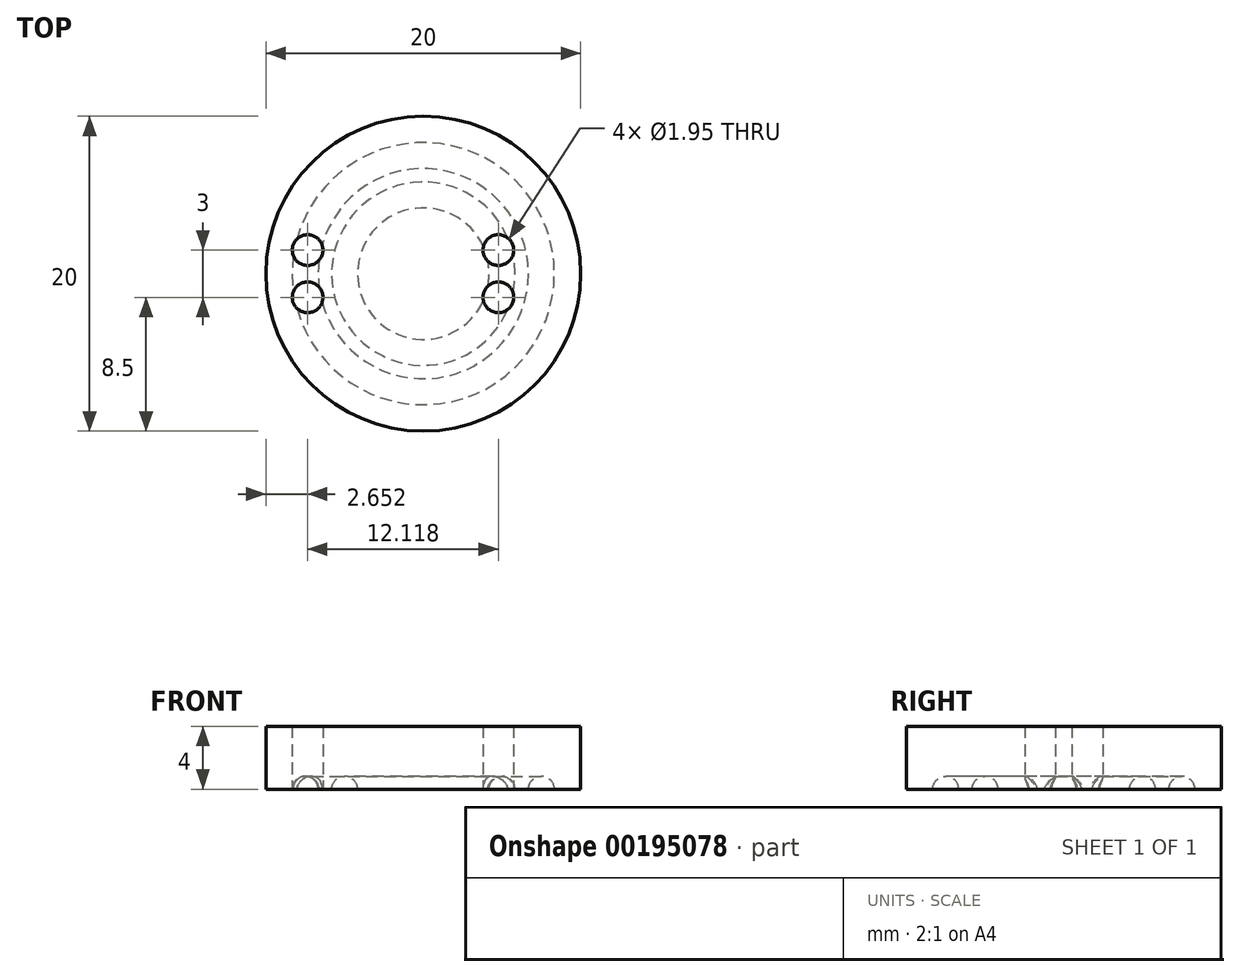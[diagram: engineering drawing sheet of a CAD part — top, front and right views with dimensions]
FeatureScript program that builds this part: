
annotation { "Feature Type Name" : "Feature", "Feature Type Description" : "" }
export const myFeature = defineFeature(function(context is Context, id is Id, definition is map)
    precondition{}
    {
        {
            assignVariable(context, id + "F0", {"name" : "thick", "anyValue" : 4});
        }
        {
            var Q0;
            Q0=qCreatedBy(makeId("Top.planeOp"),FACE);
            var sketch = newSketch(context, id + "F1", { "sketchPlane" : qUnion([Q0])});
            skCircle(sketch, "E0", {"center": v(0, 0) * mm, "radius": 10 * mm});
            skSolve(sketch);
        }
        {
            var Q0;
            Q0 = qSketchRegion(id + "F1", true);
            extrude(context, id + "F2", {"entities" : qUnion([Q0]), "depth" : (getVariable(context, 'thick')) * mm});
        }
        {
            var Q0;
            Q0=makeQuery(id+"F2.opExtrude","CAP_FACE",FACE,{"disambiguationData":[OSD([sQuery(id+"F1.wireOp",EDGE,"E0")])],"isStart":true});
            var sketch = newSketch(context, id + "F3", { "sketchPlane" : qUnion([Q0])});
            skCircle(sketch, "E1", {"center": v(0, 0) * mm, "radius": 7.5 * mm});
            skCircle(sketch, "E2", {"center": v(0, 0) * mm, "radius": 5 * mm});
            skSolve(sketch);
        }
        {
            var Q0;
            Q0=qCreatedBy(makeId("Front.planeOp"),FACE);
            var sketch = newSketch(context, id + "F4", { "sketchPlane" : qUnion([Q0])});
            skCircle(sketch, "E3", {"center": v(5, 0) * mm, "radius": 0.83 * mm});
            skCircle(sketch, "E4", {"center": v(7.5, 0) * mm, "radius": 0.83 * mm});
            skLineSegment(sketch, "E5", {"start": v(0, 6.85) * mm, "end": v(0, -4.44) * mm, "construction": true});
            skLineSegment(sketch, "E6", {"start": v(11.67, 0) * mm, "end": v(-8.41, 0) * mm, "construction": true});
            skCircle(sketch, "E7", {"center": v(5, 0) * mm, "radius": 0.68 * mm, "construction": true});
            skCircle(sketch, "E8", {"center": v(7.5, 0) * mm, "radius": 0.68 * mm, "construction": true});
            skSolve(sketch);
        }
        {
            var Q0;
            Q0=makeQuery(id+"F4.imprint","IMPRINT",FACE,{"disambiguationData":[TD([[makeQuery(id+"F4.imprint","IMPRINT",EDGE,{"derivedFrom":sQuery(id+"F4.wireOp",EDGE,"E3")}),1.0]])]});
            var Q1;
            Q1=makeQuery(id+"F4.imprint","IMPRINT",FACE,{"disambiguationData":[TD([[makeQuery(id+"F4.imprint","IMPRINT",EDGE,{"derivedFrom":sQuery(id+"F4.wireOp",EDGE,"E4")}),1.0]])]});
            var Q2;
            Q2=sQuery(id+"F3.wireOp",EDGE,"E1");
            sweep(context, id + "F5", {"operationType" : NewBodyOperationType.REMOVE, "profiles" : qUnion([Q0, Q1]), "path" : qUnion([Q2])});
        }
        {
            var Q0;
            Q0=makeQuery(id+"F5.boolean.opBoolean","SPLIT",FACE,{"disambiguationData":[TD([makeQuery(id+"F5.opSweep","SWEPT_FACE",FACE,{"disambiguationData":[OSD([sQuery(id+"F3.wireOp",EDGE,"E1"),sQuery(id+"F4.wireOp",EDGE,"E3")])]})])],"derivedFrom":makeQuery(id+"F2.opExtrude","CAP_FACE",FACE,{"disambiguationData":[OSD([sQuery(id+"F1.wireOp",EDGE,"E0")])],"isStart":true})});
            var sketch = newSketch(context, id + "F6", { "sketchPlane" : qUnion([Q0])});
            skLineSegment(sketch, "E9", {"start": v(-12.07, 0) * mm, "end": v(12.46, 0) * mm, "construction": true});
            skLineSegment(sketch, "E10", {"start": v(0, 11.33) * mm, "end": v(0, -11.24) * mm, "construction": true});
            skLineSegment(sketch, "E11", {"start": v(-11.9, 3) * mm, "end": v(11.88, 3) * mm, "construction": true});
            skLineSegment(sketch, "E12", {"start": v(11.88, -3) * mm, "end": v(-11.43, -3) * mm, "construction": true});
            skCircle(sketch, "E13", {"center": v(0, 0) * mm, "radius": 7.5 * mm, "construction": true});
            skCircle(sketch, "E14", {"center": v(-7.35, 1.5) * mm, "radius": 0.98 * mm});
            skCircle(sketch, "E15", {"center": v(-7.35, -1.5) * mm, "radius": 0.98 * mm});
            skCircle(sketch, "E16", {"center": v(0, 0) * mm, "radius": 5 * mm, "construction": true});
            skCircle(sketch, "E17", {"center": v(4.77, 1.5) * mm, "radius": 0.98 * mm});
            skCircle(sketch, "E18", {"center": v(4.77, -1.5) * mm, "radius": 0.98 * mm});
            skSolve(sketch);
        }
        {
            var Q0;
            Q0 = qSketchRegion(id + "F6", true);
            var Q1;
            Q1=makeQuery(id+"F2.opExtrude","CAP_FACE",FACE,{"disambiguationData":[OSD([sQuery(id+"F1.wireOp",EDGE,"E0")])],"isStart":false});
            extrude(context, id + "F7", {"entities" : qUnion([Q0]), "operationType" : NewBodyOperationType.REMOVE, "endBound" : BoundingType.UP_TO_SURFACE, "oppositeDirection" : true, "endBoundEntityFace" : qUnion([Q1]), "depth" : 25 * mm});
        }
    });
